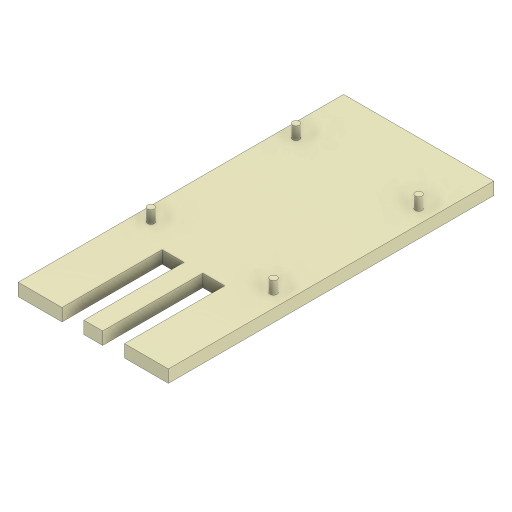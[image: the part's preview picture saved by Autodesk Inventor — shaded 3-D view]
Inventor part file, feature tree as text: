
AUTODESK INVENTOR PART (.ipt)
format: ipt  version: 2023.4 (Build 274418000, 418)  size: 200,192 bytes
history: native  units: in
note: dims shown in document units (in); Inventor stores cm internally (conversion verified against a paired STEP export)
features: sketch x5, extrude x4
ambient origin geometry x8: Origin, YZ Plane, XZ Plane, XY Plane, X Axis, Y Axis, Z Axis, Center Point
bodies: Solid1 (feature_tree)
feature tree (9):
  extrude  "Extrusion1"  Depth=2.3622in
  extrude  "Extrusion2"  Depth=1.1811in
  extrude  "Extrusion4"  Depth=0.1969in
  extrude  "Extrusion5"  Depth=0.9646in
  sketch  "Sketch9"  dims[d9=0.2953in d10=0.1063in d11=0.7874in d13=1.9291in d14=0.7874in d16=2.2835in d19=0.1969in d20=0.0in d23=1.5748in d24=0.9843in d25=0.689in d28=0.8933in d29=0.0984in d30=0.8661in d31=0.9843in d32=0.0in d39=0.2953in d40=1.5748in d41=0.1476in d42=0.0866in d43=0.0866in d44=0.0866in d45=0.0866in d47=0.0787in d48=0.0in d50=0.0in d52=0.0in d53=0.0787in d56=0.0in d57=0.1969in d58=0.0in d59=0.4921in d60=0.3346in d61=0.3346in d63=0.9394in d65=0.0787in d66=0.4921in d69=0.3725in d70=0.2165in d33=0.0197in d34=0.0344in d35=0.0197in d36=0.0344in]
  sketch  "Sketch1"  dims[d0=3.5433in d1=2.3622in]
  sketch  "Sketch2"  dims[d2=1.7717in d3=1.1811in]
  sketch  "Sketch4"  dims[d4=0.1969in d5=0.0in d6=1.9291in]
  sketch  "Sketch6"  dims[d7=2.2835in d8=0.9646in]
